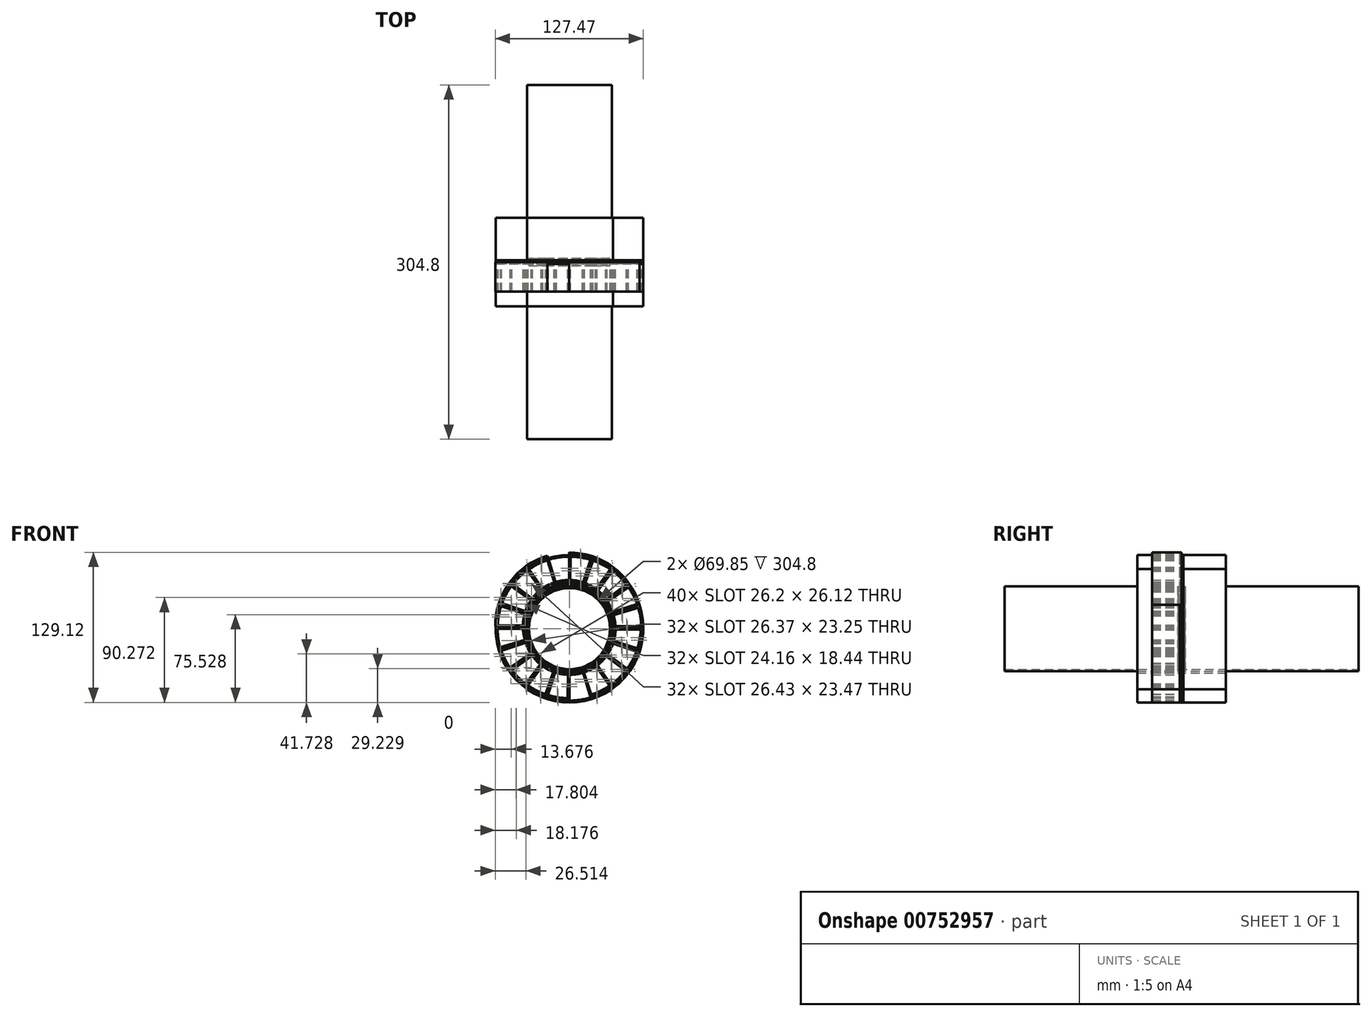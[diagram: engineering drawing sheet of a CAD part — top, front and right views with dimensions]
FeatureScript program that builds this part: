
annotation { "Feature Type Name" : "Feature", "Feature Type Description" : "" }
export const myFeature = defineFeature(function(context is Context, id is Id, definition is map)
    precondition{}
    {
        {
            var Q0;
            Q0=qCreatedBy(makeId("Front.planeOp"),FACE);
            var sketch = newSketch(context, id + "F0", { "sketchPlane" : qUnion([Q0])});
            skCircle(sketch, "E0", {"center": v(0, 0) * mm, "radius": 63.5 * mm});
            skCircle(sketch, "E1", {"center": v(0, 0) * mm, "radius": 38.1 * mm});
            skArc(sketch, "E2", {"start": v(0, 39.69) * mm, "mid": v(-5.87, 39.25) * mm, "end": v(-11.6, 37.95) * mm});
            skArc(sketch, "E3", {"start": v(0, 61.91) * mm, "mid": v(-9.15, 61.23) * mm, "end": v(-18.1, 59.2) * mm});
            skLineSegment(sketch, "E4", {"start": v(0, 39.69) * mm, "end": v(0, 61.91) * mm});
            skLineSegment(sketch, "E5.1.0", {"start": v(-12.26, 37.75) * mm, "end": v(-19.13, 58.88) * mm});
            skLineSegment(sketch, "E5.2.0", {"start": v(-23.33, 32.1) * mm, "end": v(-36.4, 50.09) * mm});
            skLineSegment(sketch, "E5.3.0", {"start": v(-32.1, 23.33) * mm, "end": v(-50.09, 36.4) * mm});
            skLineSegment(sketch, "E5.4.0", {"start": v(-37.75, 12.26) * mm, "end": v(-58.88, 19.13) * mm});
            skLineSegment(sketch, "E5.5.0", {"start": v(-39.69, 0) * mm, "end": v(-61.91, 0) * mm});
            skLineSegment(sketch, "E5.6.0", {"start": v(-37.75, -12.26) * mm, "end": v(-58.88, -19.13) * mm});
            skLineSegment(sketch, "E5.7.0", {"start": v(-32.1, -23.33) * mm, "end": v(-50.09, -36.4) * mm});
            skLineSegment(sketch, "E5.8.0", {"start": v(-23.33, -32.1) * mm, "end": v(-36.4, -50.09) * mm});
            skLineSegment(sketch, "E5.9.0", {"start": v(-12.26, -37.75) * mm, "end": v(-19.13, -58.88) * mm});
            skLineSegment(sketch, "E5.10.0", {"start": v(0, -39.69) * mm, "end": v(0, -61.91) * mm});
            skLineSegment(sketch, "E5.11.0", {"start": v(12.26, -37.75) * mm, "end": v(19.13, -58.88) * mm});
            skLineSegment(sketch, "E5.12.0", {"start": v(23.33, -32.1) * mm, "end": v(36.4, -50.09) * mm});
            skLineSegment(sketch, "E5.13.0", {"start": v(32.1, -23.33) * mm, "end": v(50.09, -36.4) * mm});
            skLineSegment(sketch, "E5.14.0", {"start": v(37.75, -12.26) * mm, "end": v(58.88, -19.13) * mm});
            skLineSegment(sketch, "E5.15.0", {"start": v(39.69, 0) * mm, "end": v(61.91, 0) * mm});
            skLineSegment(sketch, "E5.16.0", {"start": v(37.75, 12.26) * mm, "end": v(58.88, 19.13) * mm});
            skLineSegment(sketch, "E5.17.0", {"start": v(32.1, 23.33) * mm, "end": v(50.09, 36.4) * mm});
            skLineSegment(sketch, "E5.18.0", {"start": v(23.33, 32.1) * mm, "end": v(36.4, 50.09) * mm});
            skLineSegment(sketch, "E5.19.0", {"start": v(12.26, 37.75) * mm, "end": v(19.13, 58.88) * mm});
            skLineSegment(sketch, "E6.1.0", {"start": v(0.7, 39.68) * mm, "end": v(1.08, 61.9) * mm});
            skLineSegment(sketch, "E7.1.0", {"start": v(-11.6, 37.95) * mm, "end": v(-18.1, 59.2) * mm});
            skLineSegment(sketch, "E7.2.0", {"start": v(-22.76, 32.51) * mm, "end": v(-35.51, 50.72) * mm});
            skLineSegment(sketch, "E7.3.0", {"start": v(-31.7, 23.88) * mm, "end": v(-49.45, 37.26) * mm});
            skLineSegment(sketch, "E7.4.0", {"start": v(-37.53, 12.92) * mm, "end": v(-58.54, 20.16) * mm});
            skLineSegment(sketch, "E7.5.0", {"start": v(-39.68, 0.7) * mm, "end": v(-61.9, 1.08) * mm});
            skLineSegment(sketch, "E7.6.0", {"start": v(-37.95, -11.6) * mm, "end": v(-59.2, -18.1) * mm});
            skLineSegment(sketch, "E7.7.0", {"start": v(-32.51, -22.76) * mm, "end": v(-50.72, -35.51) * mm});
            skLineSegment(sketch, "E7.8.0", {"start": v(-23.88, -31.7) * mm, "end": v(-37.26, -49.45) * mm});
            skLineSegment(sketch, "E7.9.0", {"start": v(-12.92, -37.53) * mm, "end": v(-20.16, -58.54) * mm});
            skLineSegment(sketch, "E7.10.0", {"start": v(-0.7, -39.68) * mm, "end": v(-1.08, -61.9) * mm});
            skLineSegment(sketch, "E7.11.0", {"start": v(11.6, -37.95) * mm, "end": v(18.1, -59.2) * mm});
            skLineSegment(sketch, "E7.12.0", {"start": v(22.76, -32.51) * mm, "end": v(35.51, -50.72) * mm});
            skLineSegment(sketch, "E7.13.0", {"start": v(31.7, -23.88) * mm, "end": v(49.45, -37.26) * mm});
            skLineSegment(sketch, "E7.14.0", {"start": v(37.53, -12.92) * mm, "end": v(58.54, -20.16) * mm});
            skLineSegment(sketch, "E7.15.0", {"start": v(39.68, -0.7) * mm, "end": v(61.9, -1.08) * mm});
            skLineSegment(sketch, "E7.16.0", {"start": v(37.95, 11.6) * mm, "end": v(59.2, 18.1) * mm});
            skLineSegment(sketch, "E7.17.0", {"start": v(32.51, 22.76) * mm, "end": v(50.72, 35.51) * mm});
            skLineSegment(sketch, "E7.18.0", {"start": v(23.88, 31.7) * mm, "end": v(37.26, 49.45) * mm});
            skLineSegment(sketch, "E7.19.0", {"start": v(12.92, 37.53) * mm, "end": v(20.16, 58.54) * mm});
            skArc(sketch, "E8.trimOffspring", {"start": v(12.26, 37.75) * mm, "mid": v(6.55, 39.14) * mm, "end": v(0.7, 39.68) * mm});
            skArc(sketch, "E9.trimOffspring", {"start": v(19.13, 58.88) * mm, "mid": v(10.22, 61.06) * mm, "end": v(1.08, 61.9) * mm});
            skArc(sketch, "E10.trimOffspring", {"start": v(36.4, 50.09) * mm, "mid": v(28.59, 54.92) * mm, "end": v(20.16, 58.54) * mm});
            skArc(sketch, "E11.trimOffspring", {"start": v(23.33, 32.1) * mm, "mid": v(18.33, 35.2) * mm, "end": v(12.92, 37.53) * mm});
            skArc(sketch, "E12.trimOffspring", {"start": v(32.1, 23.33) * mm, "mid": v(28.3, 27.82) * mm, "end": v(23.88, 31.7) * mm});
            skArc(sketch, "E13.trimOffspring", {"start": v(50.09, 36.4) * mm, "mid": v(44.16, 43.4) * mm, "end": v(37.26, 49.45) * mm});
            skArc(sketch, "E14.trimOffspring", {"start": v(58.88, 19.13) * mm, "mid": v(55.4, 27.63) * mm, "end": v(50.72, 35.51) * mm});
            skArc(sketch, "E15.trimOffspring", {"start": v(37.75, 12.26) * mm, "mid": v(35.52, 17.7) * mm, "end": v(32.51, 22.76) * mm});
            skArc(sketch, "E16.trimOffspring", {"start": v(61.91, 0) * mm, "mid": v(61.23, 9.15) * mm, "end": v(59.2, 18.1) * mm});
            skArc(sketch, "E17.trimOffspring", {"start": v(58.88, -19.13) * mm, "mid": v(61.06, -10.22) * mm, "end": v(61.9, -1.08) * mm});
            skArc(sketch, "E18.trimOffspring", {"start": v(39.69, 0) * mm, "mid": v(39.25, 5.87) * mm, "end": v(37.95, 11.6) * mm});
            skArc(sketch, "E19.trimOffspring", {"start": v(37.75, -12.26) * mm, "mid": v(39.14, -6.55) * mm, "end": v(39.68, -0.7) * mm});
            skArc(sketch, "E20.trimOffspring", {"start": v(32.1, -23.33) * mm, "mid": v(35.2, -18.33) * mm, "end": v(37.53, -12.92) * mm});
            skArc(sketch, "E21.trimOffspring", {"start": v(50.09, -36.4) * mm, "mid": v(54.92, -28.59) * mm, "end": v(58.54, -20.16) * mm});
            skArc(sketch, "E22.trimOffspring", {"start": v(23.33, -32.1) * mm, "mid": v(27.82, -28.3) * mm, "end": v(31.7, -23.88) * mm});
            skArc(sketch, "E23.trimOffspring", {"start": v(36.4, -50.09) * mm, "mid": v(43.4, -44.16) * mm, "end": v(49.45, -37.26) * mm});
            skArc(sketch, "E24.trimOffspring", {"start": v(19.13, -58.88) * mm, "mid": v(27.63, -55.4) * mm, "end": v(35.51, -50.72) * mm});
            skArc(sketch, "E25.trimOffspring", {"start": v(12.26, -37.75) * mm, "mid": v(17.7, -35.52) * mm, "end": v(22.76, -32.51) * mm});
            skArc(sketch, "E26.trimOffspring", {"start": v(0, -39.69) * mm, "mid": v(5.87, -39.25) * mm, "end": v(11.6, -37.95) * mm});
            skArc(sketch, "E27.trimOffspring", {"start": v(0, -61.91) * mm, "mid": v(9.15, -61.23) * mm, "end": v(18.1, -59.2) * mm});
            skArc(sketch, "E28.trimOffspring", {"start": v(-19.13, -58.88) * mm, "mid": v(-10.22, -61.06) * mm, "end": v(-1.08, -61.9) * mm});
            skArc(sketch, "E29.trimOffspring", {"start": v(-12.26, -37.75) * mm, "mid": v(-6.55, -39.14) * mm, "end": v(-0.7, -39.68) * mm});
            skArc(sketch, "E30.trimOffspring", {"start": v(-23.33, -32.1) * mm, "mid": v(-18.33, -35.2) * mm, "end": v(-12.92, -37.53) * mm});
            skArc(sketch, "E31.trimOffspring", {"start": v(-32.1, -23.33) * mm, "mid": v(-28.3, -27.82) * mm, "end": v(-23.88, -31.7) * mm});
            skArc(sketch, "E32.trimOffspring", {"start": v(-36.4, -50.09) * mm, "mid": v(-28.59, -54.92) * mm, "end": v(-20.16, -58.54) * mm});
            skArc(sketch, "E33.trimOffspring", {"start": v(-50.09, -36.4) * mm, "mid": v(-44.16, -43.4) * mm, "end": v(-37.26, -49.45) * mm});
            skArc(sketch, "E34.trimOffspring", {"start": v(-61.91, 0) * mm, "mid": v(-61.23, -9.15) * mm, "end": v(-59.2, -18.1) * mm});
            skArc(sketch, "E35.trimOffspring", {"start": v(-58.88, -19.13) * mm, "mid": v(-55.4, -27.63) * mm, "end": v(-50.72, -35.51) * mm});
            skArc(sketch, "E36.trimOffspring", {"start": v(-37.75, -12.26) * mm, "mid": v(-35.52, -17.7) * mm, "end": v(-32.51, -22.76) * mm});
            skArc(sketch, "E37.trimOffspring", {"start": v(-39.69, 0) * mm, "mid": v(-39.25, -5.87) * mm, "end": v(-37.95, -11.6) * mm});
            skArc(sketch, "E38.trimOffspring", {"start": v(-37.75, 12.26) * mm, "mid": v(-39.14, 6.55) * mm, "end": v(-39.68, 0.7) * mm});
            skArc(sketch, "E39.trimOffspring", {"start": v(-19.13, 58.88) * mm, "mid": v(-27.63, 55.4) * mm, "end": v(-35.51, 50.72) * mm});
            skArc(sketch, "E40.trimOffspring", {"start": v(-36.4, 50.09) * mm, "mid": v(-43.4, 44.16) * mm, "end": v(-49.45, 37.26) * mm});
            skArc(sketch, "E41.trimOffspring", {"start": v(-50.09, 36.4) * mm, "mid": v(-54.92, 28.59) * mm, "end": v(-58.54, 20.16) * mm});
            skArc(sketch, "E42.trimOffspring", {"start": v(-58.88, 19.13) * mm, "mid": v(-61.06, 10.22) * mm, "end": v(-61.9, 1.08) * mm});
            skArc(sketch, "E43.trimOffspring", {"start": v(-23.33, 32.1) * mm, "mid": v(-27.82, 28.3) * mm, "end": v(-31.7, 23.88) * mm});
            skArc(sketch, "E44.trimOffspring", {"start": v(-12.26, 37.75) * mm, "mid": v(-17.7, 35.52) * mm, "end": v(-22.76, 32.51) * mm});
            skArc(sketch, "E45.trimOffspring", {"start": v(-32.1, 23.33) * mm, "mid": v(-35.2, 18.33) * mm, "end": v(-37.53, 12.92) * mm});
            skSolve(sketch);
        }
        {
            var Q0;
            Q0 = qSketchRegion(id + "F0", true);
            extrude(context, id + "F1", {"entities" : qUnion([Q0]), "endBound" : BoundingType.SYMMETRIC, "depth" : 76.2 * mm, "offsetDistance" : 25.4 * mm});
        }
        {
            var Q0;
            Q0=qCreatedBy(makeId("Front.planeOp"),FACE);
            var sketch = newSketch(context, id + "F2", { "sketchPlane" : qUnion([Q0])});
            skCircle(sketch, "E46", {"center": v(0, 0) * mm, "radius": 63.5 * mm});
            skArc(sketch, "E47", {"start": v(-21.85, 31.2) * mm, "mid": v(-38.1, 0.33) * mm, "end": v(-22.4, -30.82) * mm});
            skLineSegment(sketch, "E48.2.0", {"start": v(-23.33, 32.1) * mm, "end": v(-36.4, 50.09) * mm});
            skLineSegment(sketch, "E48.3.0", {"start": v(-32.1, 23.33) * mm, "end": v(-50.09, 36.4) * mm});
            skLineSegment(sketch, "E48.4.0", {"start": v(-37.75, 12.26) * mm, "end": v(-58.88, 19.13) * mm});
            skLineSegment(sketch, "E48.5.0", {"start": v(-39.69, 0) * mm, "end": v(-61.91, 0) * mm});
            skLineSegment(sketch, "E48.6.0", {"start": v(-37.75, -12.26) * mm, "end": v(-58.88, -19.13) * mm});
            skLineSegment(sketch, "E48.7.0", {"start": v(-32.1, -23.33) * mm, "end": v(-50.09, -36.4) * mm});
            skLineSegment(sketch, "E48.8.0", {"start": v(-22.4, -30.82) * mm, "end": v(-36.4, -50.09) * mm});
            skLineSegment(sketch, "E48.12.0", {"start": v(23.33, -32.1) * mm, "end": v(36.4, -50.09) * mm});
            skLineSegment(sketch, "E48.13.0", {"start": v(32.1, -23.33) * mm, "end": v(50.09, -36.4) * mm});
            skLineSegment(sketch, "E48.14.0", {"start": v(37.75, -12.26) * mm, "end": v(58.88, -19.13) * mm});
            skLineSegment(sketch, "E48.15.0", {"start": v(39.69, 0) * mm, "end": v(61.91, 0) * mm});
            skLineSegment(sketch, "E48.16.0", {"start": v(37.75, 12.26) * mm, "end": v(58.88, 19.13) * mm});
            skLineSegment(sketch, "E48.17.0", {"start": v(32.1, 23.33) * mm, "end": v(50.09, 36.4) * mm});
            skLineSegment(sketch, "E48.18.0", {"start": v(22.4, 30.82) * mm, "end": v(36.4, 50.09) * mm});
            skLineSegment(sketch, "E49.2.0", {"start": v(-21.85, 31.2) * mm, "end": v(-35.51, 50.72) * mm});
            skLineSegment(sketch, "E49.3.0", {"start": v(-31.7, 23.88) * mm, "end": v(-49.45, 37.26) * mm});
            skLineSegment(sketch, "E49.4.0", {"start": v(-37.53, 12.92) * mm, "end": v(-58.54, 20.16) * mm});
            skLineSegment(sketch, "E49.5.0", {"start": v(-39.68, 0.7) * mm, "end": v(-61.9, 1.08) * mm});
            skLineSegment(sketch, "E49.6.0", {"start": v(-37.95, -11.6) * mm, "end": v(-59.2, -18.1) * mm});
            skLineSegment(sketch, "E49.7.0", {"start": v(-32.51, -22.76) * mm, "end": v(-50.72, -35.51) * mm});
            skLineSegment(sketch, "E49.8.0", {"start": v(-23.88, -31.7) * mm, "end": v(-37.26, -49.45) * mm});
            skLineSegment(sketch, "E49.12.0", {"start": v(21.85, -31.2) * mm, "end": v(35.51, -50.72) * mm});
            skLineSegment(sketch, "E49.13.0", {"start": v(31.7, -23.88) * mm, "end": v(49.45, -37.26) * mm});
            skLineSegment(sketch, "E49.14.0", {"start": v(37.53, -12.92) * mm, "end": v(58.54, -20.16) * mm});
            skLineSegment(sketch, "E49.15.0", {"start": v(39.68, -0.7) * mm, "end": v(61.9, -1.08) * mm});
            skLineSegment(sketch, "E49.16.0", {"start": v(37.95, 11.6) * mm, "end": v(59.2, 18.1) * mm});
            skLineSegment(sketch, "E49.17.0", {"start": v(32.51, 22.76) * mm, "end": v(50.72, 35.51) * mm});
            skLineSegment(sketch, "E49.18.0", {"start": v(23.88, 31.7) * mm, "end": v(37.26, 49.45) * mm});
            skArc(sketch, "E50.trimOffspring", {"start": v(36.4, 50.09) * mm, "mid": v(0.54, 61.91) * mm, "end": v(-35.51, 50.72) * mm});
            skArc(sketch, "E51.trimOffspring", {"start": v(32.1, 23.33) * mm, "mid": v(28.3, 27.82) * mm, "end": v(23.88, 31.7) * mm});
            skArc(sketch, "E52.trimOffspring", {"start": v(50.09, 36.4) * mm, "mid": v(44.16, 43.4) * mm, "end": v(37.26, 49.45) * mm});
            skArc(sketch, "E53.trimOffspring", {"start": v(37.75, 12.26) * mm, "mid": v(35.52, 17.7) * mm, "end": v(32.51, 22.76) * mm});
            skArc(sketch, "E54.trimOffspring", {"start": v(61.91, 0) * mm, "mid": v(61.23, 9.15) * mm, "end": v(59.2, 18.1) * mm});
            skArc(sketch, "E55.trimOffspring", {"start": v(58.88, -19.13) * mm, "mid": v(61.06, -10.22) * mm, "end": v(61.9, -1.08) * mm});
            skArc(sketch, "E56.trimOffspring", {"start": v(39.69, 0) * mm, "mid": v(39.25, 5.87) * mm, "end": v(37.95, 11.6) * mm});
            skArc(sketch, "E57.trimOffspring", {"start": v(37.75, -12.26) * mm, "mid": v(39.14, -6.55) * mm, "end": v(39.68, -0.7) * mm});
            skArc(sketch, "E58.trimOffspring", {"start": v(32.1, -23.33) * mm, "mid": v(35.2, -18.33) * mm, "end": v(37.53, -12.92) * mm});
            skArc(sketch, "E59.trimOffspring", {"start": v(50.09, -36.4) * mm, "mid": v(54.92, -28.59) * mm, "end": v(58.54, -20.16) * mm});
            skArc(sketch, "E60.trimOffspring", {"start": v(23.33, -32.1) * mm, "mid": v(27.82, -28.3) * mm, "end": v(31.7, -23.88) * mm});
            skArc(sketch, "E61.trimOffspring", {"start": v(-32.1, -23.33) * mm, "mid": v(-28.3, -27.82) * mm, "end": v(-23.88, -31.7) * mm});
            skArc(sketch, "E62.trimOffspring", {"start": v(-37.75, -12.26) * mm, "mid": v(-35.52, -17.7) * mm, "end": v(-32.51, -22.76) * mm});
            skArc(sketch, "E63.trimOffspring", {"start": v(-39.69, 0) * mm, "mid": v(-39.25, -5.87) * mm, "end": v(-37.95, -11.6) * mm});
            skArc(sketch, "E64.trimOffspring", {"start": v(-37.75, 12.26) * mm, "mid": v(-39.14, 6.55) * mm, "end": v(-39.68, 0.7) * mm});
            skArc(sketch, "E65.trimOffspring", {"start": v(-36.4, 50.09) * mm, "mid": v(-43.4, 44.16) * mm, "end": v(-49.45, 37.26) * mm});
            skArc(sketch, "E66.trimOffspring", {"start": v(-50.09, 36.4) * mm, "mid": v(-54.92, 28.59) * mm, "end": v(-58.54, 20.16) * mm});
            skArc(sketch, "E67.trimOffspring", {"start": v(-23.33, 32.1) * mm, "mid": v(-27.82, 28.3) * mm, "end": v(-31.7, 23.88) * mm});
            skArc(sketch, "E68.trimOffspring", {"start": v(-32.1, 23.33) * mm, "mid": v(-35.2, 18.33) * mm, "end": v(-37.53, 12.92) * mm});
            skPoint(sketch, "E69.orphan", {"position": v(-23.33, -32.1) * mm});
            skPoint(sketch, "E70.orphan", {"position": v(22.76, -32.51) * mm});
            skArc(sketch, "E71.trimOffspring", {"start": v(21.85, -31.2) * mm, "mid": v(38.1, -0.33) * mm, "end": v(22.4, 30.82) * mm});
            skPoint(sketch, "E72.orphan", {"position": v(-36.4, -50.09) * mm});
            skPoint(sketch, "E73.orphan", {"position": v(35.51, -50.72) * mm});
            skArc(sketch, "E74.trimOffspring", {"start": v(36.4, -50.09) * mm, "mid": v(43.4, -44.16) * mm, "end": v(49.45, -37.26) * mm});
            skArc(sketch, "E75.trimOffspring", {"start": v(58.88, 19.13) * mm, "mid": v(55.4, 27.63) * mm, "end": v(50.72, 35.51) * mm});
            skArc(sketch, "E76.trimOffspring", {"start": v(-58.88, 19.13) * mm, "mid": v(-61.06, 10.22) * mm, "end": v(-61.9, 1.08) * mm});
            skArc(sketch, "E77.trimOffspring", {"start": v(-61.91, 0) * mm, "mid": v(-61.23, -9.15) * mm, "end": v(-59.2, -18.1) * mm});
            skArc(sketch, "E78.trimOffspring", {"start": v(-58.88, -19.13) * mm, "mid": v(-55.4, -27.63) * mm, "end": v(-50.72, -35.51) * mm});
            skArc(sketch, "E79.trimOffspring", {"start": v(-50.09, -36.4) * mm, "mid": v(-44.16, -43.4) * mm, "end": v(-37.26, -49.45) * mm});
            skArc(sketch, "E80.trimOffspring", {"start": v(-36.4, -50.09) * mm, "mid": v(-0.54, -61.91) * mm, "end": v(35.51, -50.72) * mm});
            skSolve(sketch);
        }
        {
            var Q0;
            Q0=makeQuery(id+"F2.imprint","IMPRINT",FACE,{"disambiguationData":[TD([[makeQuery(id+"F2.imprint","IMPRINT",EDGE,{"derivedFrom":sQuery(id+"F2.wireOp",EDGE,"E46")}),1.0]])]});
            extrude(context, id + "F3", {"entities" : qUnion([Q0]), "endBound" : BoundingType.SYMMETRIC, "depth" : 76.2 * mm, "offsetDistance" : 25.4 * mm});
        }
        {
            var Q0;
            Q0=qCreatedBy(makeId("Front.planeOp"),FACE);
            var sketch = newSketch(context, id + "F4", { "sketchPlane" : qUnion([Q0])});
            skArc(sketch, "E81", {"start": v(-36.42, 52.02) * mm, "mid": v(-63.5, 0.55) * mm, "end": v(-37.32, -51.37) * mm});
            skCircle(sketch, "E82", {"center": v(0, 0) * mm, "radius": 38.1 * mm});
            skLineSegment(sketch, "E83.2.0", {"start": v(-23.33, 32.1) * mm, "end": v(-36.4, 50.09) * mm});
            skLineSegment(sketch, "E83.3.0", {"start": v(-32.1, 23.33) * mm, "end": v(-50.09, 36.4) * mm});
            skLineSegment(sketch, "E83.4.0", {"start": v(-37.75, 12.26) * mm, "end": v(-58.88, 19.13) * mm});
            skLineSegment(sketch, "E83.5.0", {"start": v(-39.69, 0) * mm, "end": v(-61.91, 0) * mm});
            skLineSegment(sketch, "E83.6.0", {"start": v(-37.75, -12.26) * mm, "end": v(-58.88, -19.13) * mm});
            skLineSegment(sketch, "E83.7.0", {"start": v(-32.1, -23.33) * mm, "end": v(-50.09, -36.4) * mm});
            skLineSegment(sketch, "E83.8.0", {"start": v(-23.33, -32.1) * mm, "end": v(-37.32, -51.37) * mm});
            skLineSegment(sketch, "E83.12.0", {"start": v(23.33, -32.1) * mm, "end": v(36.4, -50.09) * mm});
            skLineSegment(sketch, "E83.13.0", {"start": v(32.1, -23.33) * mm, "end": v(50.09, -36.4) * mm});
            skLineSegment(sketch, "E83.14.0", {"start": v(37.75, -12.26) * mm, "end": v(58.88, -19.13) * mm});
            skLineSegment(sketch, "E83.15.0", {"start": v(39.69, 0) * mm, "end": v(61.91, 0) * mm});
            skLineSegment(sketch, "E83.16.0", {"start": v(37.75, 12.26) * mm, "end": v(58.88, 19.13) * mm});
            skLineSegment(sketch, "E83.17.0", {"start": v(32.1, 23.33) * mm, "end": v(50.09, 36.4) * mm});
            skLineSegment(sketch, "E83.18.0", {"start": v(23.33, 32.1) * mm, "end": v(37.32, 51.37) * mm});
            skLineSegment(sketch, "E84.2.0", {"start": v(-22.76, 32.51) * mm, "end": v(-36.42, 52.02) * mm});
            skLineSegment(sketch, "E84.3.0", {"start": v(-31.7, 23.88) * mm, "end": v(-49.45, 37.26) * mm});
            skLineSegment(sketch, "E84.4.0", {"start": v(-37.53, 12.92) * mm, "end": v(-58.54, 20.16) * mm});
            skLineSegment(sketch, "E84.5.0", {"start": v(-39.68, 0.7) * mm, "end": v(-61.9, 1.08) * mm});
            skLineSegment(sketch, "E84.6.0", {"start": v(-37.95, -11.6) * mm, "end": v(-59.2, -18.1) * mm});
            skLineSegment(sketch, "E84.7.0", {"start": v(-32.51, -22.76) * mm, "end": v(-50.72, -35.51) * mm});
            skLineSegment(sketch, "E84.8.0", {"start": v(-23.88, -31.7) * mm, "end": v(-37.26, -49.45) * mm});
            skLineSegment(sketch, "E84.12.0", {"start": v(22.76, -32.51) * mm, "end": v(36.42, -52.02) * mm});
            skLineSegment(sketch, "E84.13.0", {"start": v(31.7, -23.88) * mm, "end": v(49.45, -37.26) * mm});
            skLineSegment(sketch, "E84.14.0", {"start": v(37.53, -12.92) * mm, "end": v(58.54, -20.16) * mm});
            skLineSegment(sketch, "E84.15.0", {"start": v(39.68, -0.7) * mm, "end": v(61.9, -1.08) * mm});
            skLineSegment(sketch, "E84.16.0", {"start": v(37.95, 11.6) * mm, "end": v(59.2, 18.1) * mm});
            skLineSegment(sketch, "E84.17.0", {"start": v(32.51, 22.76) * mm, "end": v(50.72, 35.51) * mm});
            skLineSegment(sketch, "E84.18.0", {"start": v(23.88, 31.7) * mm, "end": v(37.26, 49.45) * mm});
            skArc(sketch, "E85.trimOffspring", {"start": v(32.1, 23.33) * mm, "mid": v(28.3, 27.82) * mm, "end": v(23.88, 31.7) * mm});
            skArc(sketch, "E86.trimOffspring", {"start": v(50.09, 36.4) * mm, "mid": v(44.16, 43.4) * mm, "end": v(37.26, 49.45) * mm});
            skArc(sketch, "E87.trimOffspring", {"start": v(58.88, 19.13) * mm, "mid": v(55.4, 27.63) * mm, "end": v(50.72, 35.51) * mm});
            skArc(sketch, "E88.trimOffspring", {"start": v(37.75, 12.26) * mm, "mid": v(35.52, 17.7) * mm, "end": v(32.51, 22.76) * mm});
            skArc(sketch, "E89.trimOffspring", {"start": v(61.91, 0) * mm, "mid": v(61.23, 9.15) * mm, "end": v(59.2, 18.1) * mm});
            skArc(sketch, "E90.trimOffspring", {"start": v(58.88, -19.13) * mm, "mid": v(61.06, -10.22) * mm, "end": v(61.9, -1.08) * mm});
            skArc(sketch, "E91.trimOffspring", {"start": v(39.69, 0) * mm, "mid": v(39.25, 5.87) * mm, "end": v(37.95, 11.6) * mm});
            skArc(sketch, "E92.trimOffspring", {"start": v(37.75, -12.26) * mm, "mid": v(39.14, -6.55) * mm, "end": v(39.68, -0.7) * mm});
            skArc(sketch, "E93.trimOffspring", {"start": v(32.1, -23.33) * mm, "mid": v(35.2, -18.33) * mm, "end": v(37.53, -12.92) * mm});
            skArc(sketch, "E94.trimOffspring", {"start": v(50.09, -36.4) * mm, "mid": v(54.92, -28.59) * mm, "end": v(58.54, -20.16) * mm});
            skArc(sketch, "E95.trimOffspring", {"start": v(23.33, -32.1) * mm, "mid": v(27.82, -28.3) * mm, "end": v(31.7, -23.88) * mm});
            skArc(sketch, "E96.trimOffspring", {"start": v(36.4, -50.09) * mm, "mid": v(43.4, -44.16) * mm, "end": v(49.45, -37.26) * mm});
            skArc(sketch, "E97.trimOffspring", {"start": v(-23.33, -32.1) * mm, "mid": v(-0.35, -39.69) * mm, "end": v(22.76, -32.51) * mm});
            skArc(sketch, "E98.trimOffspring", {"start": v(-32.1, -23.33) * mm, "mid": v(-28.3, -27.82) * mm, "end": v(-23.88, -31.7) * mm});
            skArc(sketch, "E99.trimOffspring", {"start": v(-50.09, -36.4) * mm, "mid": v(-44.16, -43.4) * mm, "end": v(-37.26, -49.45) * mm});
            skArc(sketch, "E100.trimOffspring", {"start": v(-61.91, 0) * mm, "mid": v(-61.23, -9.15) * mm, "end": v(-59.2, -18.1) * mm});
            skArc(sketch, "E101.trimOffspring", {"start": v(-58.88, -19.13) * mm, "mid": v(-55.4, -27.63) * mm, "end": v(-50.72, -35.51) * mm});
            skArc(sketch, "E102.trimOffspring", {"start": v(-37.75, -12.26) * mm, "mid": v(-35.52, -17.7) * mm, "end": v(-32.51, -22.76) * mm});
            skArc(sketch, "E103.trimOffspring", {"start": v(-39.69, 0) * mm, "mid": v(-39.25, -5.87) * mm, "end": v(-37.95, -11.6) * mm});
            skArc(sketch, "E104.trimOffspring", {"start": v(-37.75, 12.26) * mm, "mid": v(-39.14, 6.55) * mm, "end": v(-39.68, 0.7) * mm});
            skArc(sketch, "E105.trimOffspring", {"start": v(-36.4, 50.09) * mm, "mid": v(-43.4, 44.16) * mm, "end": v(-49.45, 37.26) * mm});
            skArc(sketch, "E106.trimOffspring", {"start": v(-50.09, 36.4) * mm, "mid": v(-54.92, 28.59) * mm, "end": v(-58.54, 20.16) * mm});
            skArc(sketch, "E107.trimOffspring", {"start": v(-58.88, 19.13) * mm, "mid": v(-61.06, 10.22) * mm, "end": v(-61.9, 1.08) * mm});
            skArc(sketch, "E108.trimOffspring", {"start": v(-23.33, 32.1) * mm, "mid": v(-27.82, 28.3) * mm, "end": v(-31.7, 23.88) * mm});
            skArc(sketch, "E109.trimOffspring", {"start": v(23.33, 32.1) * mm, "mid": v(0.35, 39.69) * mm, "end": v(-22.76, 32.51) * mm});
            skArc(sketch, "E110.trimOffspring", {"start": v(-32.1, 23.33) * mm, "mid": v(-35.2, 18.33) * mm, "end": v(-37.53, 12.92) * mm});
            skPoint(sketch, "E111.orphan", {"position": v(-35.51, 50.72) * mm});
            skPoint(sketch, "E112.orphan", {"position": v(36.4, 50.09) * mm});
            skPoint(sketch, "E113.orphan", {"position": v(35.51, -50.72) * mm});
            skArc(sketch, "E114.trimOffspring", {"start": v(36.42, -52.02) * mm, "mid": v(63.5, -0.55) * mm, "end": v(37.32, 51.37) * mm});
            skSolve(sketch);
        }
        {
            var Q0;
            Q0=makeQuery(id+"F4.imprint","IMPRINT",FACE,{"disambiguationData":[TD([[makeQuery(id+"F4.imprint","IMPRINT",EDGE,{"derivedFrom":sQuery(id+"F4.wireOp",EDGE,"E81")}),1.0]])]});
            extrude(context, id + "F5", {"entities" : qUnion([Q0]), "endBound" : BoundingType.SYMMETRIC, "depth" : 76.2 * mm, "offsetDistance" : 25.4 * mm});
        }
        {
            var Q0;
            Q0=qCreatedBy(makeId("Front.planeOp"),FACE);
            var sketch = newSketch(context, id + "F6", { "sketchPlane" : qUnion([Q0])});
            skCircle(sketch, "E115", {"center": v(0, 0) * mm, "radius": 36.51 * mm});
            skCircle(sketch, "E116", {"center": v(0, 0) * mm, "radius": 34.93 * mm});
            skSolve(sketch);
        }
        {
            var Q0;
            Q0=makeQuery(id+"F6.imprint","IMPRINT",FACE,{"disambiguationData":[TD([[makeQuery(id+"F6.imprint","IMPRINT",EDGE,{"derivedFrom":sQuery(id+"F6.wireOp",EDGE,"E115")}),1.0]])]});
            extrude(context, id + "F7", {"entities" : qUnion([Q0]), "endBound" : BoundingType.SYMMETRIC, "depth" : 304.8 * mm, "offsetDistance" : 25.4 * mm});
        }
        {
            var Q0;
            Q0=qCreatedBy(makeId("Front.planeOp"),FACE);
            var sketch = newSketch(context, id + "F8", { "sketchPlane" : qUnion([Q0])});
            skArc(sketch, "E117", {"start": v(-20.9, 29.94) * mm, "mid": v(-36.51, 0.33) * mm, "end": v(-21.44, -29.56) * mm});
            skArc(sketch, "E118", {"start": v(-20, 28.64) * mm, "mid": v(-34.92, 0.31) * mm, "end": v(-20.5, -28.27) * mm});
            skLineSegment(sketch, "E119", {"start": v(-20.9, 29.94) * mm, "end": v(-20, 28.64) * mm});
            skLineSegment(sketch, "E120", {"start": v(21.5, 29.51) * mm, "end": v(20.56, 28.23) * mm});
            skLineSegment(sketch, "E121", {"start": v(-21.44, -29.56) * mm, "end": v(-20.5, -28.27) * mm});
            skLineSegment(sketch, "E122", {"start": v(20.98, -29.88) * mm, "end": v(20.07, -28.58) * mm});
            skArc(sketch, "E123.trimOffspring", {"start": v(20.07, -28.58) * mm, "mid": v(34.92, -0.3) * mm, "end": v(20.56, 28.23) * mm});
            skArc(sketch, "E124.trimOffspring", {"start": v(20.98, -29.88) * mm, "mid": v(36.51, -0.32) * mm, "end": v(21.5, 29.51) * mm});
            skSolve(sketch);
        }
        {
            var Q0;
            Q0=makeQuery(id+"F8.imprint","IMPRINT",FACE,{"disambiguationData":[TD([[makeQuery(id+"F8.imprint","IMPRINT",EDGE,{"derivedFrom":sQuery(id+"F8.wireOp",EDGE,"E117")}),1.0]])]});
            var Q1;
            Q1=makeQuery(id+"F8.imprint","IMPRINT",FACE,{"disambiguationData":[TD([[makeQuery(id+"F8.imprint","IMPRINT",EDGE,{"derivedFrom":sQuery(id+"F8.wireOp",EDGE,"E120")}),1.0]])]});
            extrude(context, id + "F9", {"entities" : qUnion([Q0, Q1]), "endBound" : BoundingType.SYMMETRIC, "depth" : 76.2 * mm, "offsetDistance" : 25.4 * mm});
        }
        {
            var Q0;
            Q0=qCreatedBy(makeId("Front.planeOp"),FACE);
            var sketch = newSketch(context, id + "F10", { "sketchPlane" : qUnion([Q0])});
            skArc(sketch, "E125", {"start": v(-19.94, 28.67) * mm, "mid": v(-34.92, 0.36) * mm, "end": v(-20.53, -28.25) * mm});
            skArc(sketch, "E126", {"start": v(21.53, 29.5) * mm, "mid": v(0.42, 36.51) * mm, "end": v(-20.85, 29.98) * mm});
            skLineSegment(sketch, "E127", {"start": v(-19.94, 28.67) * mm, "end": v(-20.85, 29.98) * mm});
            skLineSegment(sketch, "E128", {"start": v(-20.85, 29.98) * mm, "end": v(-19.94, 28.67) * mm});
            skLineSegment(sketch, "E129", {"start": v(21.53, 29.5) * mm, "end": v(20.59, 28.21) * mm});
            skLineSegment(sketch, "E130", {"start": v(20.09, -28.57) * mm, "end": v(21, -29.87) * mm});
            skLineSegment(sketch, "E131", {"start": v(-21.46, -29.54) * mm, "end": v(-20.53, -28.25) * mm});
            skArc(sketch, "E132.trimOffspring", {"start": v(-21.46, -29.54) * mm, "mid": v(-0.29, -36.51) * mm, "end": v(21, -29.87) * mm});
            skArc(sketch, "E133.trimOffspring", {"start": v(20.09, -28.57) * mm, "mid": v(34.92, -0.3) * mm, "end": v(20.59, 28.21) * mm});
            skSolve(sketch);
        }
        {
            var Q0;
            Q0=makeQuery(id+"F10.imprint","IMPRINT",FACE,{"disambiguationData":[TD([[makeQuery(id+"F10.imprint","IMPRINT",EDGE,{"derivedFrom":sQuery(id+"F10.wireOp",EDGE,"E125")}),1.0]])]});
            extrude(context, id + "F11", {"entities" : qUnion([Q0]), "endBound" : BoundingType.SYMMETRIC, "depth" : 6.35 * mm, "offsetDistance" : 25.4 * mm});
        }
        {
            var Q0;
            Q0=qCreatedBy(makeId("Front.planeOp"),FACE);
            var sketch = newSketch(context, id + "F12", { "sketchPlane" : qUnion([Q0])});
            skCircle(sketch, "E134", {"center": v(0, 0) * mm, "radius": 63.5 * mm});
            skCircle(sketch, "E135", {"center": v(0, 0) * mm, "radius": 38.1 * mm});
            skSolve(sketch);
        }
        {
            var Q0;
            Q0=makeQuery(id+"F12.imprint","IMPRINT",FACE,{"disambiguationData":[TD([[makeQuery(id+"F12.imprint","IMPRINT",EDGE,{"derivedFrom":sQuery(id+"F12.wireOp",EDGE,"E134")}),1.0]])]});
            extrude(context, id + "F13", {"entities" : qUnion([Q0]), "endBound" : BoundingType.SYMMETRIC, "depth" : 3.17 * mm, "offsetDistance" : 25.4 * mm});
        }
        {
            var Q0;
            Q0=qCreatedBy(makeId("Front.planeOp"),FACE);
            var sketch = newSketch(context, id + "F14", { "sketchPlane" : qUnion([Q0])});
            skArc(sketch, "E136", {"start": v(0, 63.5) * mm, "mid": v(-51.04, 37.77) * mm, "end": v(-60.73, -18.57) * mm});
            skArc(sketch, "E137", {"start": v(-11.14, 36.44) * mm, "mid": v(-30.63, 22.66) * mm, "end": v(-38.1, 0) * mm});
            skLineSegment(sketch, "E138", {"start": v(0, 38.1) * mm, "end": v(0, 61.91) * mm});
            skLineSegment(sketch, "E139.1.0", {"start": v(-12.26, 37.75) * mm, "end": v(-19.13, 58.88) * mm});
            skLineSegment(sketch, "E139.2.0", {"start": v(-23.33, 32.1) * mm, "end": v(-36.4, 50.09) * mm});
            skLineSegment(sketch, "E139.3.0", {"start": v(-32.1, 23.33) * mm, "end": v(-50.09, 36.4) * mm});
            skLineSegment(sketch, "E139.4.0", {"start": v(-37.75, 12.26) * mm, "end": v(-58.88, 19.13) * mm});
            skLineSegment(sketch, "E139.5.0", {"start": v(-38.1, 0) * mm, "end": v(-61.91, 0) * mm});
            skLineSegment(sketch, "E139.6.0", {"start": v(-37.75, -12.26) * mm, "end": v(-58.88, -19.13) * mm});
            skLineSegment(sketch, "E139.7.0", {"start": v(-32.1, -23.33) * mm, "end": v(-50.09, -36.4) * mm});
            skLineSegment(sketch, "E139.8.0", {"start": v(-23.33, -32.1) * mm, "end": v(-36.4, -50.09) * mm});
            skLineSegment(sketch, "E139.9.0", {"start": v(-12.26, -37.75) * mm, "end": v(-19.13, -58.88) * mm});
            skLineSegment(sketch, "E139.10.0", {"start": v(0, -38.1) * mm, "end": v(0, -61.91) * mm});
            skLineSegment(sketch, "E139.11.0", {"start": v(12.26, -37.75) * mm, "end": v(19.13, -58.88) * mm});
            skLineSegment(sketch, "E139.12.0", {"start": v(23.33, -32.1) * mm, "end": v(36.4, -50.09) * mm});
            skLineSegment(sketch, "E139.13.0", {"start": v(32.1, -23.33) * mm, "end": v(50.09, -36.4) * mm});
            skLineSegment(sketch, "E139.14.0", {"start": v(37.75, -12.26) * mm, "end": v(58.88, -19.13) * mm});
            skLineSegment(sketch, "E139.15.0", {"start": v(38.1, 0) * mm, "end": v(61.91, 0) * mm});
            skLineSegment(sketch, "E139.16.0", {"start": v(37.75, 12.26) * mm, "end": v(58.88, 19.13) * mm});
            skLineSegment(sketch, "E139.17.0", {"start": v(32.1, 23.33) * mm, "end": v(50.09, 36.4) * mm});
            skLineSegment(sketch, "E139.18.0", {"start": v(23.33, 32.1) * mm, "end": v(36.4, 50.09) * mm});
            skLineSegment(sketch, "E139.19.0", {"start": v(12.26, 37.75) * mm, "end": v(19.13, 58.88) * mm});
            skLineSegment(sketch, "E140.1.0", {"start": v(0.7, 39.68) * mm, "end": v(1.08, 61.9) * mm});
            skLineSegment(sketch, "E141.1.0", {"start": v(-11.14, 36.44) * mm, "end": v(-18.1, 59.2) * mm});
            skLineSegment(sketch, "E141.2.0", {"start": v(-22.76, 32.51) * mm, "end": v(-35.51, 50.72) * mm});
            skLineSegment(sketch, "E141.3.0", {"start": v(-31.7, 23.88) * mm, "end": v(-49.45, 37.26) * mm});
            skLineSegment(sketch, "E141.4.0", {"start": v(-37.53, 12.92) * mm, "end": v(-58.54, 20.16) * mm});
            skLineSegment(sketch, "E141.5.0", {"start": v(-39.68, 0.7) * mm, "end": v(-61.9, 1.08) * mm});
            skLineSegment(sketch, "E141.6.0", {"start": v(-36.44, -11.14) * mm, "end": v(-59.2, -18.1) * mm});
            skLineSegment(sketch, "E141.7.0", {"start": v(-32.51, -22.76) * mm, "end": v(-50.72, -35.51) * mm});
            skLineSegment(sketch, "E141.8.0", {"start": v(-23.88, -31.7) * mm, "end": v(-37.26, -49.45) * mm});
            skLineSegment(sketch, "E141.9.0", {"start": v(-12.92, -37.53) * mm, "end": v(-20.16, -58.54) * mm});
            skLineSegment(sketch, "E141.10.0", {"start": v(-0.7, -39.68) * mm, "end": v(-1.08, -61.9) * mm});
            skLineSegment(sketch, "E141.11.0", {"start": v(11.14, -36.44) * mm, "end": v(18.1, -59.2) * mm});
            skLineSegment(sketch, "E141.12.0", {"start": v(22.76, -32.51) * mm, "end": v(35.51, -50.72) * mm});
            skLineSegment(sketch, "E141.13.0", {"start": v(31.7, -23.88) * mm, "end": v(49.45, -37.26) * mm});
            skLineSegment(sketch, "E141.14.0", {"start": v(37.53, -12.92) * mm, "end": v(58.54, -20.16) * mm});
            skLineSegment(sketch, "E141.15.0", {"start": v(39.68, -0.7) * mm, "end": v(61.9, -1.08) * mm});
            skLineSegment(sketch, "E141.16.0", {"start": v(36.44, 11.14) * mm, "end": v(59.2, 18.1) * mm});
            skLineSegment(sketch, "E141.17.0", {"start": v(32.51, 22.76) * mm, "end": v(50.72, 35.51) * mm});
            skLineSegment(sketch, "E141.18.0", {"start": v(23.88, 31.7) * mm, "end": v(37.26, 49.45) * mm});
            skLineSegment(sketch, "E141.19.0", {"start": v(12.92, 37.53) * mm, "end": v(20.16, 58.54) * mm});
            skArc(sketch, "E142.trimOffspring", {"start": v(12.26, 37.75) * mm, "mid": v(6.55, 39.14) * mm, "end": v(0.7, 39.68) * mm});
            skArc(sketch, "E143.trimOffspring", {"start": v(19.13, 58.88) * mm, "mid": v(10.22, 61.06) * mm, "end": v(1.08, 61.9) * mm});
            skArc(sketch, "E144.trimOffspring", {"start": v(36.4, 50.09) * mm, "mid": v(28.59, 54.92) * mm, "end": v(20.16, 58.54) * mm});
            skArc(sketch, "E145.trimOffspring", {"start": v(23.33, 32.1) * mm, "mid": v(18.33, 35.2) * mm, "end": v(12.92, 37.53) * mm});
            skArc(sketch, "E146.trimOffspring", {"start": v(32.1, 23.33) * mm, "mid": v(28.3, 27.82) * mm, "end": v(23.88, 31.7) * mm});
            skArc(sketch, "E147.trimOffspring", {"start": v(50.09, 36.4) * mm, "mid": v(44.16, 43.4) * mm, "end": v(37.26, 49.45) * mm});
            skArc(sketch, "E148.trimOffspring", {"start": v(58.88, 19.13) * mm, "mid": v(55.4, 27.63) * mm, "end": v(50.72, 35.51) * mm});
            skArc(sketch, "E149.trimOffspring", {"start": v(37.75, 12.26) * mm, "mid": v(35.52, 17.7) * mm, "end": v(32.51, 22.76) * mm});
            skArc(sketch, "E150.trimOffspring", {"start": v(58.88, -19.13) * mm, "mid": v(61.06, -10.22) * mm, "end": v(61.9, -1.08) * mm});
            skArc(sketch, "E151.trimOffspring", {"start": v(37.75, -12.26) * mm, "mid": v(39.14, -6.55) * mm, "end": v(39.68, -0.7) * mm});
            skArc(sketch, "E152.trimOffspring", {"start": v(32.1, -23.33) * mm, "mid": v(35.2, -18.33) * mm, "end": v(37.53, -12.92) * mm});
            skArc(sketch, "E153.trimOffspring", {"start": v(50.09, -36.4) * mm, "mid": v(54.92, -28.59) * mm, "end": v(58.54, -20.16) * mm});
            skArc(sketch, "E154.trimOffspring", {"start": v(23.33, -32.1) * mm, "mid": v(27.82, -28.3) * mm, "end": v(31.7, -23.88) * mm});
            skArc(sketch, "E155.trimOffspring", {"start": v(36.4, -50.09) * mm, "mid": v(43.4, -44.16) * mm, "end": v(49.45, -37.26) * mm});
            skArc(sketch, "E156.trimOffspring", {"start": v(0, -61.91) * mm, "mid": v(9.15, -61.23) * mm, "end": v(18.1, -59.2) * mm});
            skArc(sketch, "E157.trimOffspring", {"start": v(12.26, -37.75) * mm, "mid": v(17.7, -35.52) * mm, "end": v(22.76, -32.51) * mm});
            skArc(sketch, "E158.trimOffspring", {"start": v(-19.13, -58.88) * mm, "mid": v(-10.22, -61.06) * mm, "end": v(-1.08, -61.9) * mm});
            skArc(sketch, "E159.trimOffspring", {"start": v(-12.26, -37.75) * mm, "mid": v(-6.55, -39.14) * mm, "end": v(-0.7, -39.68) * mm});
            skArc(sketch, "E160.trimOffspring", {"start": v(-23.33, -32.1) * mm, "mid": v(-18.33, -35.2) * mm, "end": v(-12.92, -37.53) * mm});
            skArc(sketch, "E161.trimOffspring", {"start": v(-32.1, -23.33) * mm, "mid": v(-28.3, -27.82) * mm, "end": v(-23.88, -31.7) * mm});
            skArc(sketch, "E162.trimOffspring", {"start": v(-36.4, -50.09) * mm, "mid": v(-28.59, -54.92) * mm, "end": v(-20.16, -58.54) * mm});
            skArc(sketch, "E163.trimOffspring", {"start": v(-50.09, -36.4) * mm, "mid": v(-44.16, -43.4) * mm, "end": v(-37.26, -49.45) * mm});
            skArc(sketch, "E164.trimOffspring", {"start": v(-58.88, -19.13) * mm, "mid": v(-55.4, -27.63) * mm, "end": v(-50.72, -35.51) * mm});
            skArc(sketch, "E165.trimOffspring", {"start": v(-37.75, -12.26) * mm, "mid": v(-35.52, -17.7) * mm, "end": v(-32.51, -22.76) * mm});
            skArc(sketch, "E166.trimOffspring", {"start": v(-37.75, 12.26) * mm, "mid": v(-39.14, 6.55) * mm, "end": v(-39.68, 0.7) * mm});
            skArc(sketch, "E167.trimOffspring", {"start": v(-19.13, 58.88) * mm, "mid": v(-27.63, 55.4) * mm, "end": v(-35.51, 50.72) * mm});
            skArc(sketch, "E168.trimOffspring", {"start": v(-36.4, 50.09) * mm, "mid": v(-43.4, 44.16) * mm, "end": v(-49.45, 37.26) * mm});
            skArc(sketch, "E169.trimOffspring", {"start": v(-50.09, 36.4) * mm, "mid": v(-54.92, 28.59) * mm, "end": v(-58.54, 20.16) * mm});
            skArc(sketch, "E170.trimOffspring", {"start": v(-58.88, 19.13) * mm, "mid": v(-61.06, 10.22) * mm, "end": v(-61.9, 1.08) * mm});
            skArc(sketch, "E171.trimOffspring", {"start": v(-23.33, 32.1) * mm, "mid": v(-27.82, 28.3) * mm, "end": v(-31.7, 23.88) * mm});
            skArc(sketch, "E172.trimOffspring", {"start": v(-12.26, 37.75) * mm, "mid": v(-17.7, 35.52) * mm, "end": v(-22.76, 32.51) * mm});
            skArc(sketch, "E173.trimOffspring", {"start": v(-32.1, 23.33) * mm, "mid": v(-35.2, 18.33) * mm, "end": v(-37.53, 12.92) * mm});
            skPoint(sketch, "E174.orphan", {"position": v(-61.91, 0) * mm});
            skPoint(sketch, "E175.orphan", {"position": v(-39.69, 0) * mm});
            skPoint(sketch, "E176.orphan", {"position": v(-37.95, -11.6) * mm});
            skPoint(sketch, "E177.orphan", {"position": v(-59.2, -18.1) * mm});
            skPoint(sketch, "E178.orphan", {"position": v(18.1, -59.2) * mm});
            skPoint(sketch, "E179.orphan", {"position": v(11.6, -37.95) * mm});
            skPoint(sketch, "E180.orphan", {"position": v(0, -39.69) * mm});
            skPoint(sketch, "E181.orphan", {"position": v(0, -61.91) * mm});
            skPoint(sketch, "E182.orphan", {"position": v(59.2, 18.1) * mm});
            skPoint(sketch, "E183.orphan", {"position": v(37.95, 11.6) * mm});
            skPoint(sketch, "E184.orphan", {"position": v(61.91, 0) * mm});
            skPoint(sketch, "E185.orphan", {"position": v(39.69, 0) * mm});
            skArc(sketch, "E186.trimOffspring", {"start": v(36.44, 11.14) * mm, "mid": v(22.66, 30.63) * mm, "end": v(0, 38.1) * mm});
            skArc(sketch, "E187.trimOffspring", {"start": v(63.5, 0) * mm, "mid": v(44.9, 44.9) * mm, "end": v(0, 63.5) * mm});
            skArc(sketch, "E188.trimOffspring", {"start": v(11.14, -36.44) * mm, "mid": v(30.63, -22.66) * mm, "end": v(38.1, 0) * mm});
            skArc(sketch, "E189.trimOffspring", {"start": v(18.57, -60.73) * mm, "mid": v(51.04, -37.77) * mm, "end": v(63.5, 0) * mm});
            skArc(sketch, "E190.trimOffspring", {"start": v(-36.44, -11.14) * mm, "mid": v(-22.66, -30.63) * mm, "end": v(0, -38.1) * mm});
            skArc(sketch, "E191.trimOffspring", {"start": v(-60.73, -18.57) * mm, "mid": v(-29.81, -56.07) * mm, "end": v(18.57, -60.73) * mm});
            skArc(sketch, "E192.trimOffspring", {"start": v(0, 61.91) * mm, "mid": v(-9.15, 61.23) * mm, "end": v(-18.1, 59.2) * mm});
            skArc(sketch, "E193.trimOffspring", {"start": v(61.91, 0) * mm, "mid": v(61.23, 9.15) * mm, "end": v(59.2, 18.1) * mm});
            skArc(sketch, "E194.trimOffspring", {"start": v(19.13, -58.88) * mm, "mid": v(27.63, -55.4) * mm, "end": v(35.51, -50.72) * mm});
            skArc(sketch, "E195.trimOffspring", {"start": v(-61.91, 0) * mm, "mid": v(-61.23, -9.15) * mm, "end": v(-59.2, -18.1) * mm});
            skSolve(sketch);
        }
        {
            var Q0;
            Q0 = qSketchRegion(id + "F14", true);
            var Q1;
            Q1=makeQuery(id+"F14.imprint","IMPRINT",FACE,{"disambiguationData":[TD([[makeQuery(id+"F14.imprint","IMPRINT",EDGE,{"derivedFrom":sQuery(id+"F14.wireOp",EDGE,"E136")}),1.0]])]});
            extrude(context, id + "F15", {"entities" : qUnion([Q0, Q1]), "depth" : 25.4 * mm, "offsetDistance" : 25.4 * mm});
        }
        {
            var Q0;
            Q0=qCreatedBy(makeId("Front.planeOp"),FACE);
            var sketch = newSketch(context, id + "F16", { "sketchPlane" : qUnion([Q0])});
            skArc(sketch, "E196", {"start": v(-19.04, 62.84) * mm, "mid": v(-51.51, 39.89) * mm, "end": v(-63.97, 2.12) * mm});
            skArc(sketch, "E197", {"start": v(-0.47, 40.22) * mm, "mid": v(-27.41, 29.06) * mm, "end": v(-38.57, 2.12) * mm});
            skLineSegment(sketch, "E198", {"start": v(-0.47, 41.8) * mm, "end": v(-0.47, 65.62) * mm});
            skLineSegment(sketch, "E199.1.0", {"start": v(-12.73, 39.86) * mm, "end": v(-19.6, 61) * mm});
            skLineSegment(sketch, "E199.2.0", {"start": v(-23.8, 34.22) * mm, "end": v(-36.86, 52.2) * mm});
            skLineSegment(sketch, "E199.3.0", {"start": v(-32.58, 25.44) * mm, "end": v(-50.56, 38.5) * mm});
            skLineSegment(sketch, "E199.4.0", {"start": v(-38.22, 14.38) * mm, "end": v(-59.35, 21.25) * mm});
            skLineSegment(sketch, "E199.5.0", {"start": v(-40.16, 2.12) * mm, "end": v(-63.97, 2.12) * mm});
            skLineSegment(sketch, "E199.6.0", {"start": v(-38.22, -10.15) * mm, "end": v(-59.35, -17.02) * mm});
            skLineSegment(sketch, "E199.7.0", {"start": v(-32.58, -21.21) * mm, "end": v(-50.56, -34.28) * mm});
            skLineSegment(sketch, "E199.8.0", {"start": v(-23.8, -30) * mm, "end": v(-36.86, -47.97) * mm});
            skLineSegment(sketch, "E199.9.0", {"start": v(-12.73, -35.63) * mm, "end": v(-19.6, -56.77) * mm});
            skLineSegment(sketch, "E199.10.0", {"start": v(-0.47, -37.57) * mm, "end": v(-0.47, -61.38) * mm});
            skLineSegment(sketch, "E199.11.0", {"start": v(11.8, -35.63) * mm, "end": v(18.66, -56.77) * mm});
            skLineSegment(sketch, "E199.12.0", {"start": v(22.86, -30) * mm, "end": v(35.92, -47.97) * mm});
            skLineSegment(sketch, "E199.13.0", {"start": v(31.64, -21.21) * mm, "end": v(49.62, -34.28) * mm});
            skLineSegment(sketch, "E199.14.0", {"start": v(37.27, -10.15) * mm, "end": v(58.41, -17.02) * mm});
            skLineSegment(sketch, "E199.15.0", {"start": v(39.22, 2.12) * mm, "end": v(63.03, 2.12) * mm});
            skLineSegment(sketch, "E199.16.0", {"start": v(37.27, 14.38) * mm, "end": v(58.41, 21.25) * mm});
            skLineSegment(sketch, "E199.17.0", {"start": v(31.64, 25.44) * mm, "end": v(49.62, 38.5) * mm});
            skLineSegment(sketch, "E199.18.0", {"start": v(22.86, 34.22) * mm, "end": v(35.92, 52.2) * mm});
            skLineSegment(sketch, "E199.19.0", {"start": v(11.8, 39.86) * mm, "end": v(18.66, 61) * mm});
            skLineSegment(sketch, "E200.1.0", {"start": v(0.22, 41.8) * mm, "end": v(0.61, 64.02) * mm});
            skLineSegment(sketch, "E201.1.0", {"start": v(-12.07, 40.07) * mm, "end": v(-19.04, 62.84) * mm});
            skLineSegment(sketch, "E201.2.0", {"start": v(-23.23, 34.63) * mm, "end": v(-35.98, 52.83) * mm});
            skLineSegment(sketch, "E201.3.0", {"start": v(-32.17, 26) * mm, "end": v(-49.92, 39.38) * mm});
            skLineSegment(sketch, "E201.4.0", {"start": v(-38, 15.04) * mm, "end": v(-59, 22.27) * mm});
            skLineSegment(sketch, "E201.5.0", {"start": v(-40.15, 2.8) * mm, "end": v(-62.37, 3.2) * mm});
            skLineSegment(sketch, "E201.6.0", {"start": v(-38.42, -9.49) * mm, "end": v(-61.2, -16.45) * mm});
            skLineSegment(sketch, "E201.7.0", {"start": v(-32.98, -20.65) * mm, "end": v(-51.19, -33.4) * mm});
            skLineSegment(sketch, "E201.8.0", {"start": v(-24.35, -29.58) * mm, "end": v(-37.73, -47.33) * mm});
            skLineSegment(sketch, "E201.9.0", {"start": v(-13.4, -35.4) * mm, "end": v(-20.63, -56.42) * mm});
            skLineSegment(sketch, "E201.10.0", {"start": v(-1.16, -37.57) * mm, "end": v(-1.55, -59.79) * mm});
            skLineSegment(sketch, "E201.11.0", {"start": v(11.13, -35.84) * mm, "end": v(18.1, -58.6) * mm});
            skLineSegment(sketch, "E201.12.0", {"start": v(22.3, -30.4) * mm, "end": v(35.04, -48.6) * mm});
            skLineSegment(sketch, "E201.13.0", {"start": v(31.23, -21.77) * mm, "end": v(48.98, -35.14) * mm});
            skLineSegment(sketch, "E201.14.0", {"start": v(37.06, -10.8) * mm, "end": v(58.07, -18.04) * mm});
            skLineSegment(sketch, "E201.15.0", {"start": v(39.21, 1.42) * mm, "end": v(61.43, 1.04) * mm});
            skLineSegment(sketch, "E201.16.0", {"start": v(37.48, 13.72) * mm, "end": v(60.26, 20.68) * mm});
            skLineSegment(sketch, "E201.17.0", {"start": v(32.04, 24.88) * mm, "end": v(50.25, 37.63) * mm});
            skLineSegment(sketch, "E201.18.0", {"start": v(23.41, 33.81) * mm, "end": v(36.79, 51.56) * mm});
            skLineSegment(sketch, "E201.19.0", {"start": v(12.45, 39.64) * mm, "end": v(19.69, 60.66) * mm});
            skArc(sketch, "E202.trimOffspring", {"start": v(11.8, 39.86) * mm, "mid": v(6.08, 41.26) * mm, "end": v(0.22, 41.8) * mm});
            skArc(sketch, "E203.trimOffspring", {"start": v(18.66, 61) * mm, "mid": v(9.75, 63.18) * mm, "end": v(0.61, 64.02) * mm});
            skArc(sketch, "E204.trimOffspring", {"start": v(35.92, 52.2) * mm, "mid": v(28.12, 57.03) * mm, "end": v(19.69, 60.66) * mm});
            skArc(sketch, "E205.trimOffspring", {"start": v(22.86, 34.22) * mm, "mid": v(17.86, 37.32) * mm, "end": v(12.45, 39.64) * mm});
            skArc(sketch, "E206.trimOffspring", {"start": v(31.64, 25.44) * mm, "mid": v(27.84, 29.93) * mm, "end": v(23.41, 33.81) * mm});
            skArc(sketch, "E207.trimOffspring", {"start": v(49.62, 38.5) * mm, "mid": v(43.69, 45.51) * mm, "end": v(36.79, 51.56) * mm});
            skArc(sketch, "E208.trimOffspring", {"start": v(58.41, 21.25) * mm, "mid": v(54.94, 29.74) * mm, "end": v(50.25, 37.63) * mm});
            skArc(sketch, "E209.trimOffspring", {"start": v(39.22, 2.12) * mm, "mid": v(38.78, 7.98) * mm, "end": v(37.48, 13.72) * mm});
            skArc(sketch, "E210.trimOffspring", {"start": v(58.41, -17.02) * mm, "mid": v(60.6, -8.1) * mm, "end": v(61.43, 1.04) * mm});
            skArc(sketch, "E211.trimOffspring", {"start": v(37.27, -10.15) * mm, "mid": v(38.67, -4.43) * mm, "end": v(39.21, 1.42) * mm});
            skArc(sketch, "E212.trimOffspring", {"start": v(31.64, -21.21) * mm, "mid": v(34.73, -16.21) * mm, "end": v(37.06, -10.8) * mm});
            skArc(sketch, "E213.trimOffspring", {"start": v(49.62, -34.28) * mm, "mid": v(54.45, -26.47) * mm, "end": v(58.07, -18.04) * mm});
            skArc(sketch, "E214.trimOffspring", {"start": v(22.86, -30) * mm, "mid": v(27.35, -26.2) * mm, "end": v(31.23, -21.77) * mm});
            skArc(sketch, "E215.trimOffspring", {"start": v(35.92, -47.97) * mm, "mid": v(42.92, -42.04) * mm, "end": v(48.98, -35.14) * mm});
            skArc(sketch, "E216.trimOffspring", {"start": v(11.8, -35.63) * mm, "mid": v(17.24, -33.4) * mm, "end": v(22.3, -30.4) * mm});
            skArc(sketch, "E217.trimOffspring", {"start": v(-19.6, -56.77) * mm, "mid": v(-10.69, -58.95) * mm, "end": v(-1.55, -59.79) * mm});
            skArc(sketch, "E218.trimOffspring", {"start": v(-12.73, -35.63) * mm, "mid": v(-7.02, -37.03) * mm, "end": v(-1.16, -37.57) * mm});
            skArc(sketch, "E219.trimOffspring", {"start": v(-23.8, -30) * mm, "mid": v(-18.8, -33.09) * mm, "end": v(-13.4, -35.4) * mm});
            skArc(sketch, "E220.trimOffspring", {"start": v(-32.58, -21.21) * mm, "mid": v(-28.78, -25.7) * mm, "end": v(-24.35, -29.58) * mm});
            skArc(sketch, "E221.trimOffspring", {"start": v(-36.86, -47.97) * mm, "mid": v(-29.06, -52.8) * mm, "end": v(-20.63, -56.42) * mm});
            skArc(sketch, "E222.trimOffspring", {"start": v(-50.56, -34.28) * mm, "mid": v(-44.63, -41.28) * mm, "end": v(-37.73, -47.33) * mm});
            skArc(sketch, "E223.trimOffspring", {"start": v(-59.35, -17.02) * mm, "mid": v(-55.88, -25.5) * mm, "end": v(-51.19, -33.4) * mm});
            skArc(sketch, "E224.trimOffspring", {"start": v(-40.16, 2.12) * mm, "mid": v(-39.72, -3.75) * mm, "end": v(-38.42, -9.49) * mm});
            skArc(sketch, "E225.trimOffspring", {"start": v(-38.22, 14.38) * mm, "mid": v(-39.61, 8.67) * mm, "end": v(-40.15, 2.8) * mm});
            skArc(sketch, "E226.trimOffspring", {"start": v(-19.6, 61) * mm, "mid": v(-28.1, 57.52) * mm, "end": v(-35.98, 52.83) * mm});
            skArc(sketch, "E227.trimOffspring", {"start": v(-36.86, 52.2) * mm, "mid": v(-43.87, 46.27) * mm, "end": v(-49.92, 39.38) * mm});
            skArc(sketch, "E228.trimOffspring", {"start": v(-50.56, 38.5) * mm, "mid": v(-55.39, 30.7) * mm, "end": v(-59, 22.27) * mm});
            skArc(sketch, "E229.trimOffspring", {"start": v(-59.35, 21.25) * mm, "mid": v(-61.53, 12.33) * mm, "end": v(-62.37, 3.2) * mm});
            skArc(sketch, "E230.trimOffspring", {"start": v(-23.8, 34.22) * mm, "mid": v(-28.29, 30.42) * mm, "end": v(-32.17, 26) * mm});
            skArc(sketch, "E231.trimOffspring", {"start": v(-0.47, 41.8) * mm, "mid": v(-6.34, 41.37) * mm, "end": v(-12.07, 40.07) * mm});
            skArc(sketch, "E232.trimOffspring", {"start": v(-32.58, 25.44) * mm, "mid": v(-35.67, 20.44) * mm, "end": v(-38, 15.04) * mm});
            skPoint(sketch, "E233.orphan", {"position": v(-62.38, 2.12) * mm});
            skPoint(sketch, "E234.orphan", {"position": v(-40.16, 2.12) * mm});
            skPoint(sketch, "E235.orphan", {"position": v(-38.42, -9.49) * mm});
            skPoint(sketch, "E236.orphan", {"position": v(-59.68, -15.99) * mm});
            skPoint(sketch, "E237.orphan", {"position": v(17.63, -57.1) * mm});
            skPoint(sketch, "E238.orphan", {"position": v(11.13, -35.84) * mm});
            skPoint(sketch, "E239.orphan", {"position": v(-0.47, -37.57) * mm});
            skPoint(sketch, "E240.orphan", {"position": v(-0.47, -59.8) * mm});
            skPoint(sketch, "E241.orphan", {"position": v(58.74, 20.22) * mm});
            skPoint(sketch, "E242.orphan", {"position": v(37.48, 13.72) * mm});
            skPoint(sketch, "E243.orphan", {"position": v(61.44, 2.12) * mm});
            skPoint(sketch, "E244.orphan", {"position": v(39.22, 2.12) * mm});
            skArc(sketch, "E245.trimOffspring", {"start": v(35.97, 13.26) * mm, "mid": v(22.2, 32.74) * mm, "end": v(-0.47, 40.22) * mm});
            skArc(sketch, "E246.trimOffspring", {"start": v(60.26, 20.68) * mm, "mid": v(37.3, 53.16) * mm, "end": v(-0.47, 65.62) * mm});
            skArc(sketch, "E247.trimOffspring", {"start": v(10.67, -34.32) * mm, "mid": v(33.17, -15.77) * mm, "end": v(35.97, 13.26) * mm});
            skArc(sketch, "E248.trimOffspring", {"start": v(18.1, -58.6) * mm, "mid": v(50.57, -35.66) * mm, "end": v(63.03, 2.12) * mm});
            skArc(sketch, "E249.trimOffspring", {"start": v(-38.57, 2.12) * mm, "mid": v(-23.13, -28.51) * mm, "end": v(10.67, -34.32) * mm});
            skArc(sketch, "E250.trimOffspring", {"start": v(-61.2, -16.45) * mm, "mid": v(-38.24, -48.93) * mm, "end": v(-0.47, -61.38) * mm});
            skArc(sketch, "E251.trimOffspring", {"start": v(18.66, -56.77) * mm, "mid": v(27.16, -53.3) * mm, "end": v(35.04, -48.6) * mm});
            skArc(sketch, "E252.trimOffspring", {"start": v(-38.22, -10.15) * mm, "mid": v(-35.99, -15.6) * mm, "end": v(-32.98, -20.65) * mm});
            skArc(sketch, "E253.trimOffspring", {"start": v(-12.73, 39.86) * mm, "mid": v(-18.18, 37.63) * mm, "end": v(-23.23, 34.63) * mm});
            skArc(sketch, "E254.trimOffspring", {"start": v(-0.47, -37.57) * mm, "mid": v(5.4, -37.14) * mm, "end": v(11.13, -35.84) * mm});
            skArc(sketch, "E255.trimOffspring", {"start": v(37.27, 14.38) * mm, "mid": v(35.05, 19.82) * mm, "end": v(32.04, 24.88) * mm});
            skSolve(sketch);
        }
        {
            var Q0;
            Q0 = qSketchRegion(id + "F16", true);
            var Q1;
            Q1=makeQuery(id+"F16.imprint","IMPRINT",FACE,{"disambiguationData":[TD([[makeQuery(id+"F16.imprint","IMPRINT",EDGE,{"derivedFrom":sQuery(id+"F16.wireOp",EDGE,"E196")}),1.0]])]});
            extrude(context, id + "F17", {"entities" : qUnion([Q0, Q1]), "depth" : 25.4 * mm, "offsetDistance" : 25.4 * mm});
        }
    });
